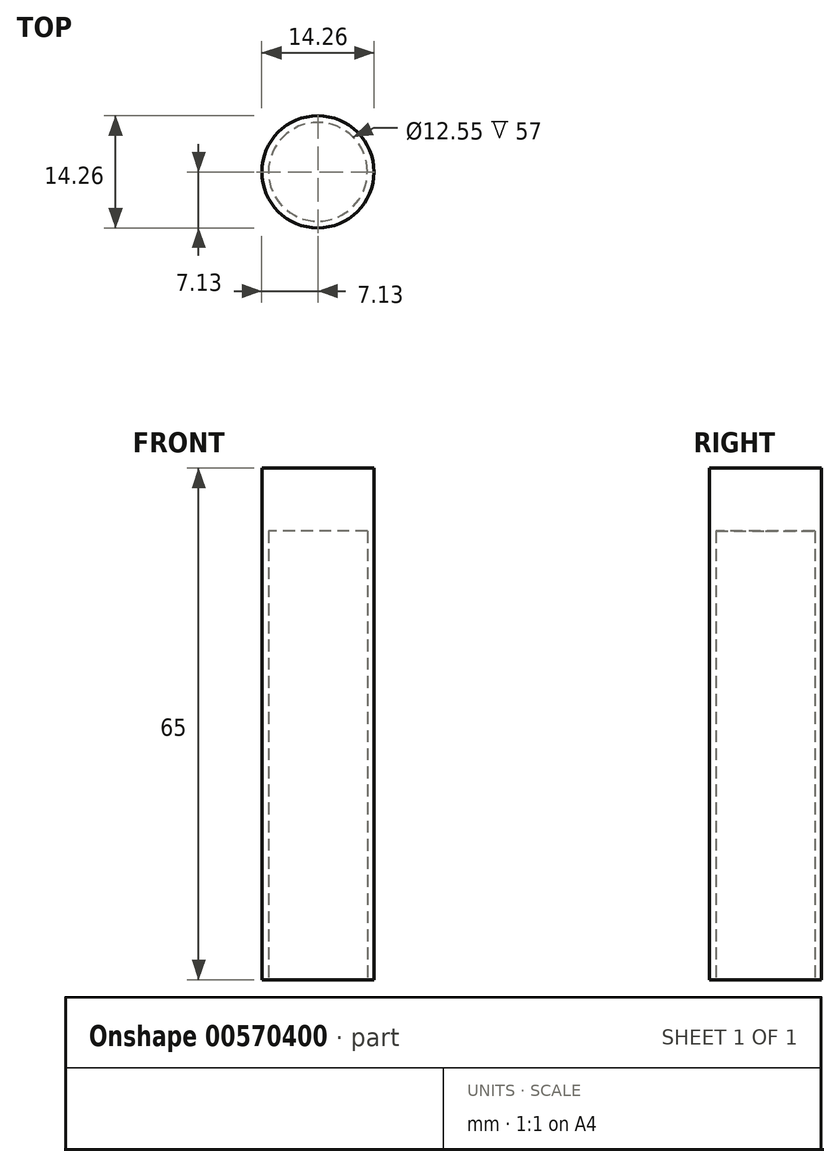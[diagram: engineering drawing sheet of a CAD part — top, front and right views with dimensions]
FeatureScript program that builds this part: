
annotation { "Feature Type Name" : "Feature", "Feature Type Description" : "" }
export const myFeature = defineFeature(function(context is Context, id is Id, definition is map)
    precondition{}
    {
        {
            var Q0;
            Q0=qCreatedBy(makeId("Top.planeOp"),FACE);
            var sketch = newSketch(context, id + "F0", { "sketchPlane" : qUnion([Q0])});
            skCircle(sketch, "E0", {"center": v(0, 0) * mm, "radius": 7.12 * mm});
            skCircle(sketch, "E1", {"center": v(0, 0) * mm, "radius": 6.28 * mm});
            skSolve(sketch);
        }
        {
            var Q0;
            Q0=makeQuery(id+"F0.imprint","IMPRINT",FACE,{"disambiguationData":[TD([[makeQuery(id+"F0.imprint","IMPRINT",EDGE,{"derivedFrom":sQuery(id+"F0.wireOp",EDGE,"E0")}),1.0]])]});
            var Q1;
            Q1=makeQuery(id+"F0.imprint","IMPRINT",FACE,{"disambiguationData":[TD([[makeQuery(id+"F0.imprint","IMPRINT",EDGE,{"derivedFrom":sQuery(id+"F0.wireOp",EDGE,"E1")}),1.0]])]});
            extrude(context, id + "F1", {"entities" : qUnion([Q0, Q1]), "depth" : 65 * mm, "offsetDistance" : 25 * mm});
        }
        {
            var Q0;
            Q0=makeQuery(id+"F0.imprint","IMPRINT",FACE,{"disambiguationData":[TD([[makeQuery(id+"F0.imprint","IMPRINT",EDGE,{"derivedFrom":sQuery(id+"F0.wireOp",EDGE,"E1")}),1.0]])]});
            extrude(context, id + "F2", {"entities" : qUnion([Q0]), "operationType" : NewBodyOperationType.REMOVE, "depth" : 57 * mm, "offsetDistance" : 25 * mm});
        }
    });
